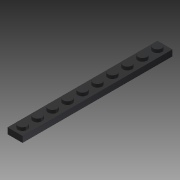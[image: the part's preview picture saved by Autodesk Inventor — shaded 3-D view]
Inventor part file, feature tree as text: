
AUTODESK INVENTOR PART (.ipt)
format: ipt  version: 2013 (Build 170138000, 138)  size: 135,680 bytes
history: native  units: mm
features: extrude x3, sketch x1, pattern_linear x1
ambient origin geometry x8: Origin, YZ Plane, XZ Plane, XY Plane, X Axis, Y Axis, Z Axis, Center Point
bodies: Solid1 (feature_tree)
feature tree (5):
  sketch  "Sketch1"  dims[d0=8.0mm d1=8.0mm d2=4.8mm d3=3.2mm d4=0.0mm d5=4.9mm d6=0.0mm d7=1.7mm d8=0.0mm d9=100.0mm d11=8.0mm d22=10.0mm d24=8.0mm]
  extrude  "Extrusion1"  Depth=8.0mm
  extrude  "Extrusion2"  Depth=4.8mm
  extrude  "Extrusion3"  Depth=3.2mm TaperAngle=0.0deg
  pattern_linear  "Rectangular Pattern1"  Spacing1=4.9mm  [1 undecoded]
note: 1 required parameter value undecoded (feature->parameter linkage not recoverable at this tier; creation-order binding heuristic only, values carry confidence <= 0.55)
